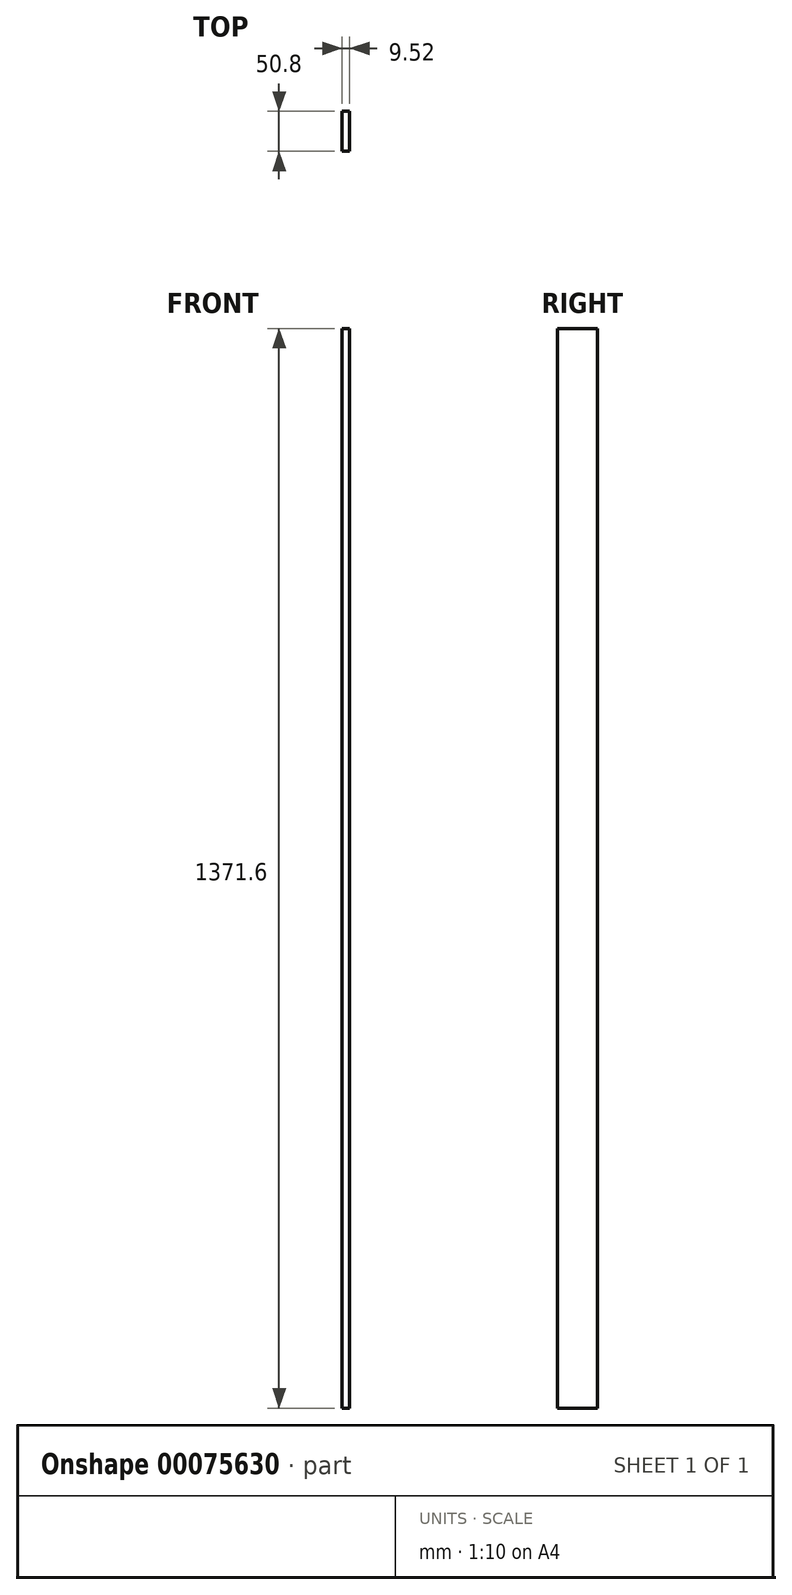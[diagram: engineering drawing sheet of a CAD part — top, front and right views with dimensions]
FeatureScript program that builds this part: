
annotation { "Feature Type Name" : "Feature", "Feature Type Description" : "" }
export const myFeature = defineFeature(function(context is Context, id is Id, definition is map)
    precondition{}
    {
        {
            var Q0;
            Q0=qCreatedBy(makeId("Top.planeOp"),FACE);
            var sketch = newSketch(context, id + "F0", { "sketchPlane" : qUnion([Q0])});
            skLineSegment(sketch, "E0.rect.bottom", {"start": v(4.76, 25.4) * mm, "end": v(-4.76, 25.4) * mm});
            skLineSegment(sketch, "E0.rect.top", {"start": v(4.76, -25.4) * mm, "end": v(-4.76, -25.4) * mm});
            skLineSegment(sketch, "E0.rect.left", {"start": v(4.76, 25.4) * mm, "end": v(4.76, -25.4) * mm});
            skLineSegment(sketch, "E0.rect.right", {"start": v(-4.76, 25.4) * mm, "end": v(-4.76, -25.4) * mm});
            skPoint(sketch, "E0.rect.middle", {"position": v(0, 0) * mm});
            skSolve(sketch);
        }
        {
            var Q0;
            Q0=qSketchRegion(id+"F0",true);
            extrude(context, id + "F1", {"entities" : qUnion([Q0]), "endBound" : BoundingType.SYMMETRIC, "depth" : 1371.6 * mm});
        }
    });
